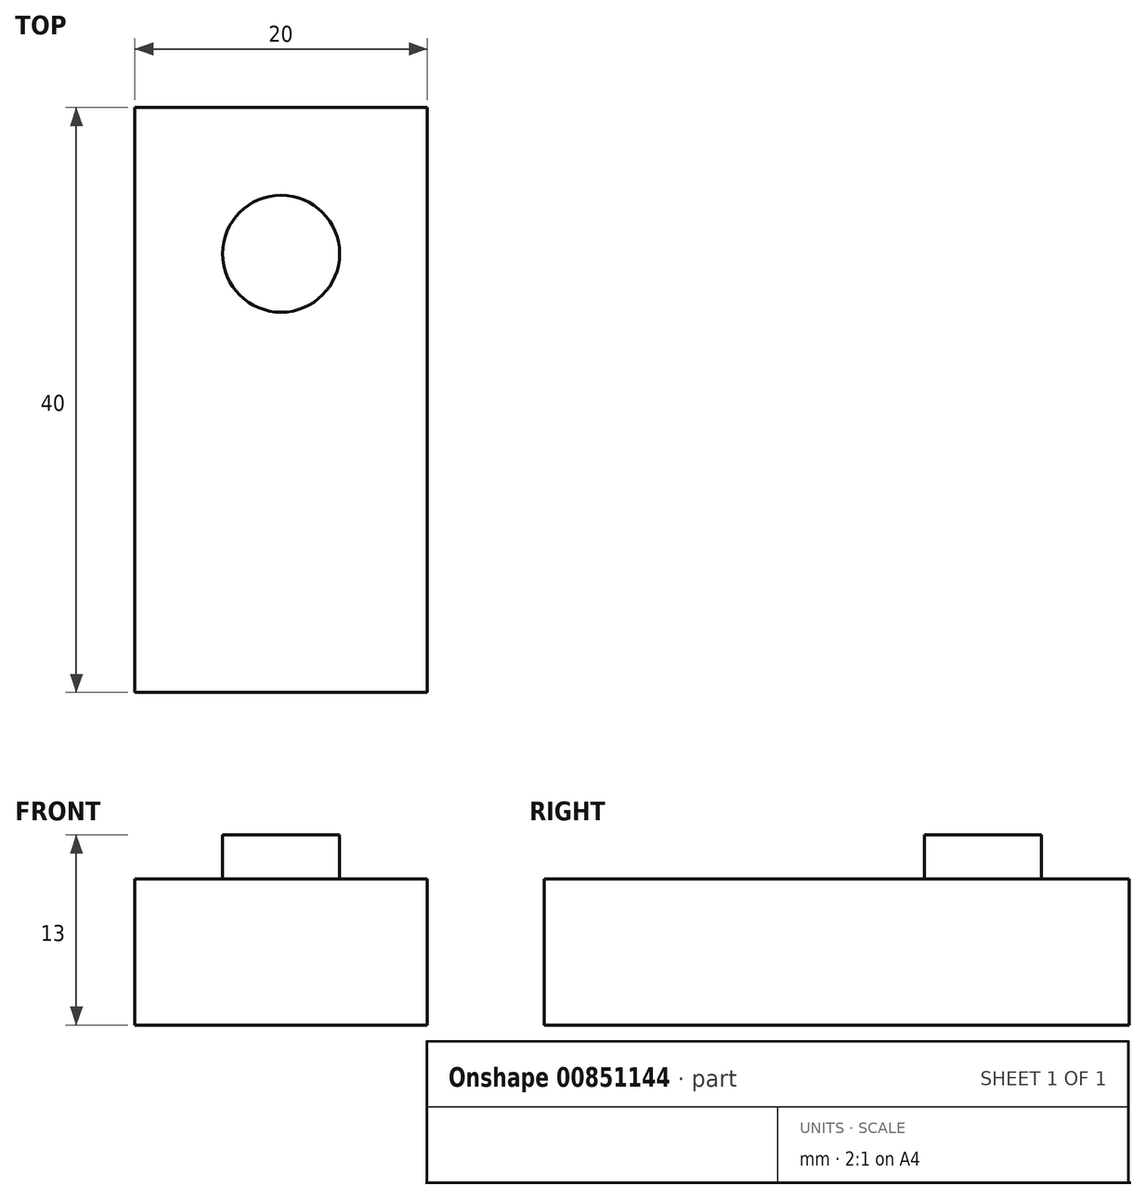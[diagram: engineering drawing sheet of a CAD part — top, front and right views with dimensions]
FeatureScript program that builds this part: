
annotation { "Feature Type Name" : "Feature", "Feature Type Description" : "" }
export const myFeature = defineFeature(function(context is Context, id is Id, definition is map)
    precondition{}
    {
        {
            var Q0;
            Q0=qCreatedBy(makeId("Front.planeOp"),FACE);
            var sketch = newSketch(context, id + "F0", { "sketchPlane" : qUnion([Q0])});
            skLineSegment(sketch, "E0.bottom", {"start": v(0, 0) * mm, "end": v(-20, 0) * mm});
            skLineSegment(sketch, "E0.top", {"start": v(0, 10) * mm, "end": v(-20, 10) * mm});
            skLineSegment(sketch, "E0.left", {"start": v(0, 0) * mm, "end": v(0, 10) * mm});
            skLineSegment(sketch, "E0.right", {"start": v(-20, 0) * mm, "end": v(-20, 10) * mm});
            skSolve(sketch);
        }
        {
            var Q0;
            Q0 = qSketchRegion(id + "F0", true);
            extrude(context, id + "F1", {"entities" : qUnion([Q0]), "depth" : 40 * mm, "offsetDistance" : 25 * mm});
        }
        {
            var Q0;
            Q0=makeQuery(id+"F1.opExtrude","SWEPT_FACE",FACE,{"disambiguationData":[OSD([sQuery(id+"F0.wireOp",EDGE,"E0.top")])]});
            var sketch = newSketch(context, id + "F2", { "sketchPlane" : qUnion([Q0])});
            skCircle(sketch, "E1", {"center": v(-10, -10) * mm, "radius": 4 * mm});
            skSolve(sketch);
        }
        {
            var Q0;
            Q0 = qSketchRegion(id + "F2", true);
            extrude(context, id + "F3", {"entities" : qUnion([Q0]), "operationType" : NewBodyOperationType.ADD, "depth" : 3 * mm, "offsetDistance" : 25 * mm});
        }
    });
